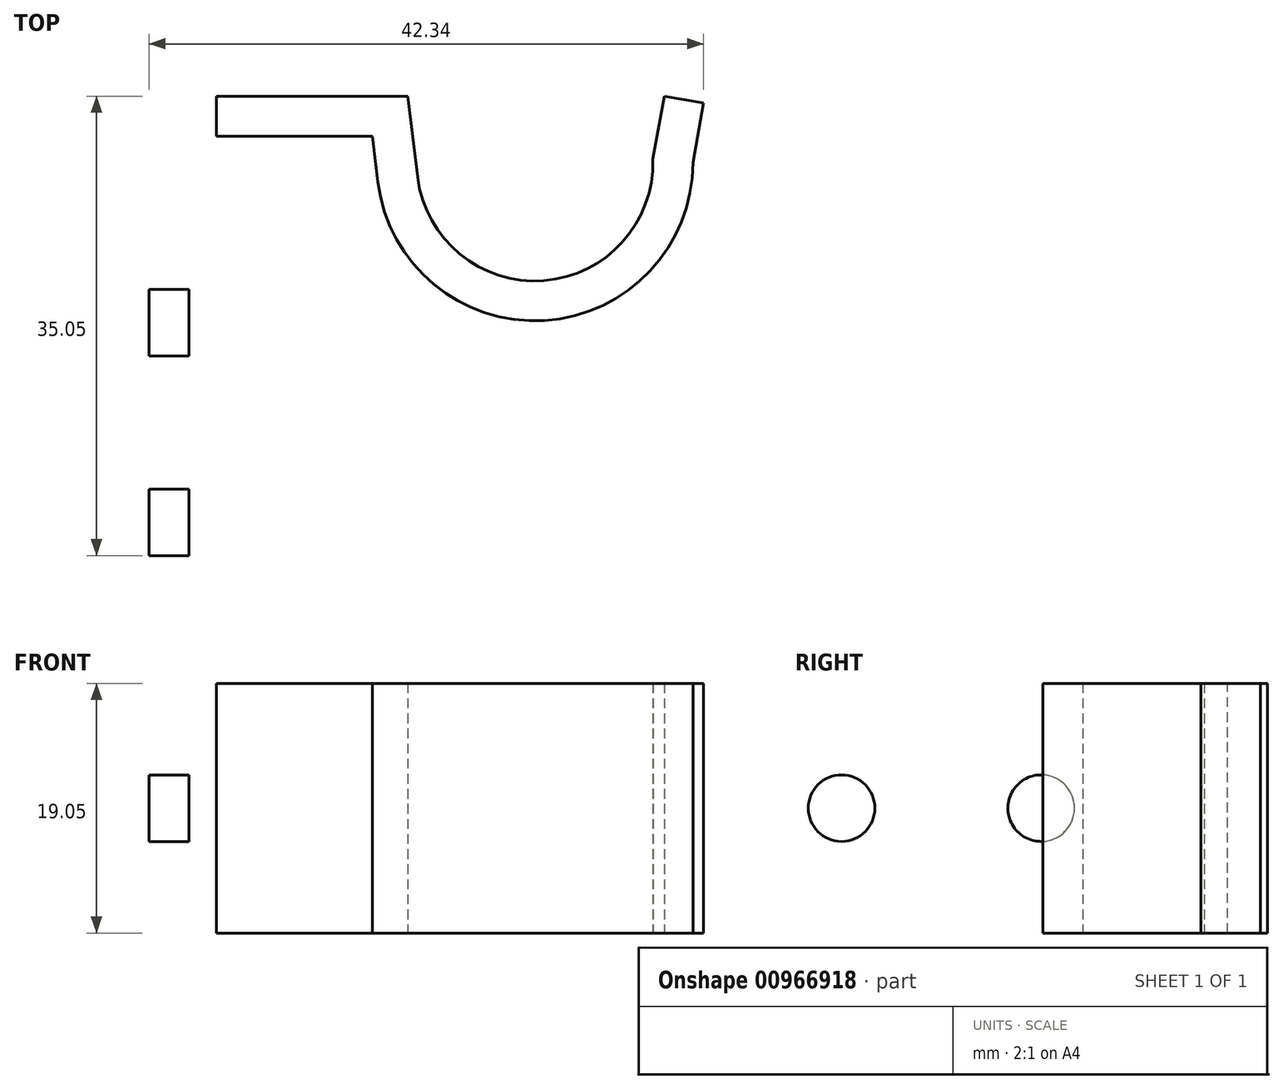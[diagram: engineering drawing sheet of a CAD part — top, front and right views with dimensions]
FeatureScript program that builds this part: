
annotation { "Feature Type Name" : "Feature", "Feature Type Description" : "" }
export const myFeature = defineFeature(function(context is Context, id is Id, definition is map)
    precondition{}
    {
        {
            var Q0;
            Q0=qCreatedBy(makeId("Top.planeOp"),FACE);
            var sketch = newSketch(context, id + "F0", { "sketchPlane" : qUnion([Q0])});
            skLineSegment(sketch, "E0", {"start": v(0, 0) * mm, "end": v(19.76, 0) * mm});
            skLineSegment(sketch, "E1", {"start": v(0, 0) * mm, "end": v(0, -38.86) * mm});
            skLineSegment(sketch, "E2", {"start": v(29.46, 0) * mm, "end": v(29.46, -5.08) * mm});
            skCircle(sketch, "E3", {"center": v(29.46, -5.08) * mm, "radius": 8.26 * mm});
            skLineSegment(sketch, "E4", {"start": v(20.51, -6.18) * mm, "end": v(19.76, 0) * mm});
            skLineSegment(sketch, "E5", {"start": v(38.48, -4.82) * mm, "end": v(39.34, 0) * mm});
            skArc(sketch, "E6", {"start": v(20.51, -6.18) * mm, "mid": v(30.14, -14.07) * mm, "end": v(38.48, -4.82) * mm});
            skArc(sketch, "E7", {"start": v(38.48, -4.82) * mm, "mid": v(28.78, 3.91) * mm, "end": v(20.51, -6.18) * mm});
            skLineSegment(sketch, "E8", {"start": v(19.76, 0) * mm, "end": v(22.01, 0) * mm});
            skLineSegment(sketch, "E9.0", {"start": v(3.05, -3.05) * mm, "end": v(3.05, -38.86) * mm});
            skLineSegment(sketch, "E9.1", {"start": v(41.53, -5.07) * mm, "end": v(42.34, -0.54) * mm});
            skArc(sketch, "E9.2", {"start": v(17.49, -6.55) * mm, "mid": v(30.2, -17.12) * mm, "end": v(41.53, -5.07) * mm});
            skLineSegment(sketch, "E9.3", {"start": v(17.49, -6.55) * mm, "end": v(17.06, -3.05) * mm});
            skLineSegment(sketch, "E9.4", {"start": v(3.05, -3.05) * mm, "end": v(17.06, -3.05) * mm});
            skLineSegment(sketch, "E10", {"start": v(3.05, -38.86) * mm, "end": v(0, -38.86) * mm});
            skLineSegment(sketch, "E11", {"start": v(42.34, -0.54) * mm, "end": v(39.34, 0) * mm});
            skLineSegment(sketch, "E12", {"start": v(22.01, 0) * mm, "end": v(29.46, 0) * mm});
            skLineSegment(sketch, "E13", {"start": v(20.45, 0) * mm, "end": v(20.45, -5.08) * mm});
            skSolve(sketch);
        }
        {
            var Q0;
            Q0=makeQuery(id+"F0.imprint","IMPRINT",FACE,{"disambiguationData":[TD([[makeQuery(id+"F0.imprint","IMPRINT",EDGE,{"derivedFrom":sQuery(id+"F0.wireOp",EDGE,"E0")}),-1.0]])]});
            var Q1;
            Q1=sQuery(id+"F0.wireOp",EDGE,"E1");
            var Q2;
            Q2=sQuery(id+"F0.wireOp",EDGE,"E0");
            var Q3;
            Q3=sQuery(id+"F0.wireOp",EDGE,"E9.0");
            var Q4;
            Q4=sQuery(id+"F0.wireOp",EDGE,"E10");
            var Q5;
            Q5=sQuery(id+"F0.wireOp",EDGE,"E9.4");
            var Q6;
            Q6=sQuery(id+"F0.wireOp",EDGE,"E9.2");
            var Q7;
            Q7=sQuery(id+"F0.wireOp",EDGE,"E4");
            var Q8;
            Q8=sQuery(id+"F0.wireOp",EDGE,"E6");
            var Q9;
            Q9=sQuery(id+"F0.wireOp",EDGE,"E5");
            var Q10;
            Q10=sQuery(id+"F0.wireOp",EDGE,"E11");
            var Q11;
            Q11=sQuery(id+"F0.wireOp",EDGE,"E9.1");
            var Q12;
            Q12=sQuery(id+"F0.wireOp",EDGE,"E9.3");
            extrude(context, id + "F1", {"entities" : qUnion([Q0]), "surfaceEntities" : qUnion([Q1, Q2, Q3, Q4, Q5, Q6, Q7, Q8, Q9, Q10, Q11, Q12]), "depth" : 19.05 * mm, "offsetDistance" : 25.4 * mm});
        }
        {
            var Q0;
            Q0=makeQuery(id+"F1.opExtrude","SWEPT_FACE",FACE,{"disambiguationData":[OSD([sQuery(id+"F0.wireOp",EDGE,"E1")])]});
            var sketch = newSketch(context, id + "F2", { "sketchPlane" : qUnion([Q0])});
            skLineSegment(sketch, "E14", {"start": v(32.51, 19.05) * mm, "end": v(32.51, 0) * mm});
            skCircle(sketch, "E15", {"center": v(32.51, 9.53) * mm, "radius": 2.54 * mm});
            skLineSegment(sketch, "E16", {"start": v(17.27, 19.05) * mm, "end": v(17.27, 0) * mm});
            skCircle(sketch, "E17", {"center": v(17.27, 9.52) * mm, "radius": 2.54 * mm});
            skSolve(sketch);
        }
        {
            var Q0;
            {var subQ0=sQuery(id+"F2.wireOp",EDGE,"E17");var subQ1=sQuery(id+"F2.wireOp",EDGE,"E16");var subQ2=makeQuery(id+"F2.imprint","INTERSECT",VERTEX,{"disambiguationData":[OD(0.0)],"derivedFrom":[subQ1,subQ0]});Q0=makeQuery(id+"F2.imprint","IMPRINT",FACE,{"disambiguationData":[TD([[makeQuery(id+"F2.imprint","IMPRINT",EDGE,{"disambiguationData":[TD([[subQ2,-1.0]])],"derivedFrom":subQ1}),1.0]])]});}
            var Q1;
            {var subQ0=sQuery(id+"F2.wireOp",EDGE,"E17");var subQ1=sQuery(id+"F2.wireOp",EDGE,"E16");var subQ2=makeQuery(id+"F2.imprint","INTERSECT",VERTEX,{"disambiguationData":[OD(0.0)],"derivedFrom":[subQ1,subQ0]});Q1=makeQuery(id+"F2.imprint","IMPRINT",FACE,{"disambiguationData":[TD([[makeQuery(id+"F2.imprint","IMPRINT",EDGE,{"disambiguationData":[TD([[subQ2,-1.0]])],"derivedFrom":subQ1}),-1.0]])]});}
            var Q2;
            {var subQ0=sQuery(id+"F2.wireOp",EDGE,"E15");var subQ1=sQuery(id+"F2.wireOp",EDGE,"E14");var subQ2=makeQuery(id+"F2.imprint","INTERSECT",VERTEX,{"disambiguationData":[OD(0.0)],"derivedFrom":[subQ1,subQ0]});Q2=makeQuery(id+"F2.imprint","IMPRINT",FACE,{"disambiguationData":[TD([[makeQuery(id+"F2.imprint","IMPRINT",EDGE,{"disambiguationData":[TD([[subQ2,-1.0]])],"derivedFrom":subQ1}),-1.0]])]});}
            var Q3;
            {var subQ0=sQuery(id+"F2.wireOp",EDGE,"E15");var subQ1=sQuery(id+"F2.wireOp",EDGE,"E14");var subQ2=makeQuery(id+"F2.imprint","INTERSECT",VERTEX,{"disambiguationData":[OD(0.0)],"derivedFrom":[subQ1,subQ0]});Q3=makeQuery(id+"F2.imprint","IMPRINT",FACE,{"disambiguationData":[TD([[makeQuery(id+"F2.imprint","IMPRINT",EDGE,{"disambiguationData":[TD([[subQ2,-1.0]])],"derivedFrom":subQ1}),1.0]])]});}
            var Q4;
            Q4=makeQuery(id+"F1.opExtrude","SWEPT_FACE",FACE,{"disambiguationData":[OSD([sQuery(id+"F0.wireOp",EDGE,"E9.0")])]});
            extrude(context, id + "F3", {"entities" : qUnion([Q0, Q1, Q2, Q3]), "operationType" : NewBodyOperationType.REMOVE, "oppositeDirection" : true, "depth" : 5.16 * mm, "offsetDistance" : 25.4 * mm, "hasSecondDirection" : true, "secondDirectionOppositeDirection" : false, "secondDirectionDepth" : 7.6 * mm, "secondDirectionBoundEntityFace" : qUnion([Q4])});
        }
    });
